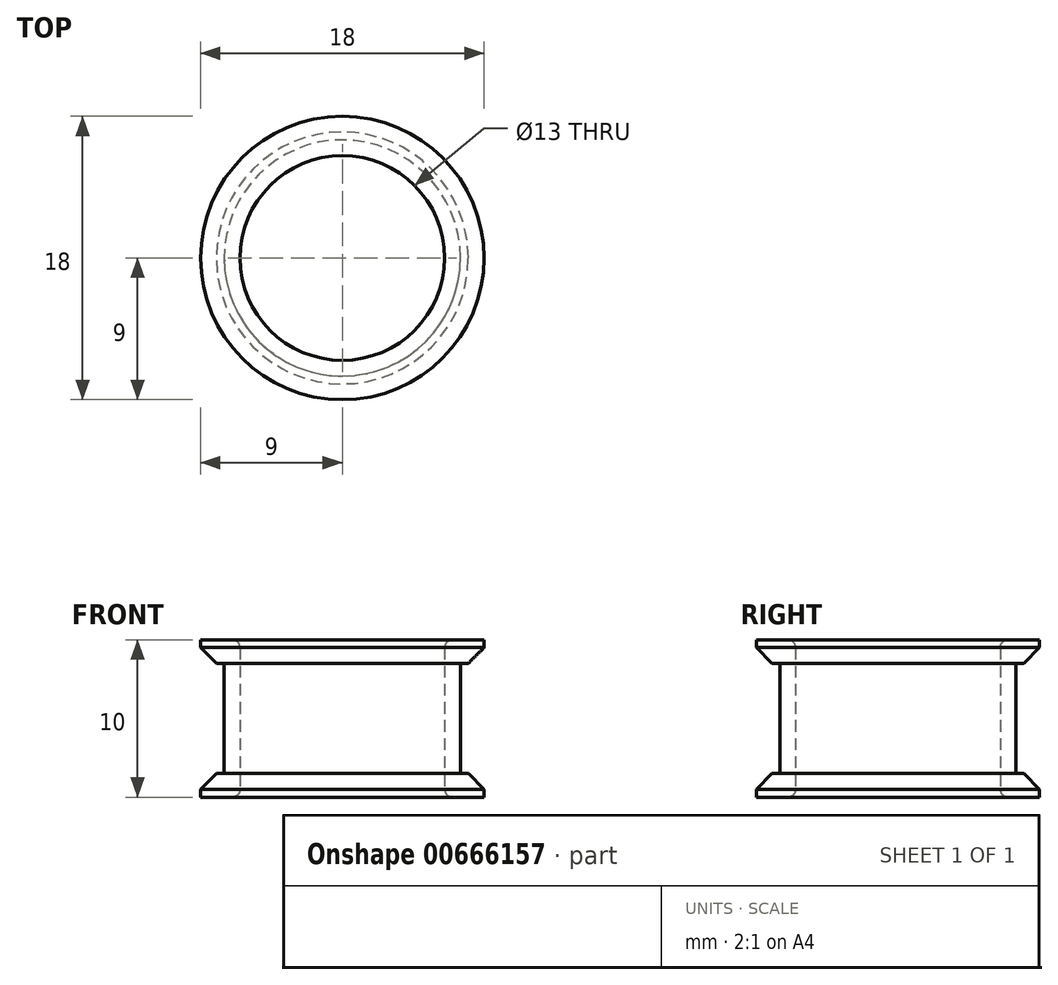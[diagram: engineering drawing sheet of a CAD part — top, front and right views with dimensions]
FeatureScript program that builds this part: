
annotation { "Feature Type Name" : "Feature", "Feature Type Description" : "" }
export const myFeature = defineFeature(function(context is Context, id is Id, definition is map)
    precondition{}
    {
        {
            var Q0;
            Q0=qCreatedBy(makeId("Top.planeOp"),FACE);
            var sketch = newSketch(context, id + "F0", { "sketchPlane" : qUnion([Q0])});
            skCircle(sketch, "E0", {"center": v(0, 0) * mm, "radius": 7.5 * mm});
            skCircle(sketch, "E1", {"center": v(0, 0) * mm, "radius": 6.5 * mm});
            skSolve(sketch);
        }
        {
            var Q0;
            Q0=makeQuery(id+"F0.imprint","IMPRINT",FACE,{"disambiguationData":[TD([[makeQuery(id+"F0.imprint","IMPRINT",EDGE,{"derivedFrom":sQuery(id+"F0.wireOp",EDGE,"E0")}),1.0]])]});
            extrude(context, id + "F1", {"entities" : qUnion([Q0]), "depth" : 10 * mm, "offsetDistance" : 25 * mm});
        }
        {
            var Q0;
            Q0=makeQuery(id+"F1.opExtrude","CAP_FACE",FACE,{"disambiguationData":[OSD([sQuery(id+"F0.wireOp",EDGE,"E0"),sQuery(id+"F0.wireOp",EDGE,"E1")])],"isStart":false});
            var sketch = newSketch(context, id + "F2", { "sketchPlane" : qUnion([Q0])});
            skCircle(sketch, "E2", {"center": v(0, 0) * mm, "radius": 9 * mm});
            skSolve(sketch);
        }
        {
            var Q0;
            Q0=makeQuery(id+"F2.imprint","IMPRINT",FACE,{"disambiguationData":[TD([[makeQuery(id+"F2.imprint","IMPRINT",EDGE,{"derivedFrom":sQuery(id+"F2.wireOp",EDGE,"E2")}),1.0]])]});
            extrude(context, id + "F3", {"entities" : qUnion([Q0]), "operationType" : NewBodyOperationType.ADD, "depth" : -1.5 * mm, "offsetDistance" : 25 * mm});
        }
        {
            var Q0;
            Q0=makeQuery(id+"F3.opExtrude","CAP_EDGE",EDGE,{"disambiguationData":[OSD([sQuery(id+"F2.wireOp",EDGE,"E2")])],"isStart":false});
            chamfer(context, id + "F4", {"entities" : qUnion([Q0]), "width" : 1 * mm, "tangentPropagation" : true});
        }
        {
            var Q0;
            Q0=makeQuery(id+"F1.opExtrude","CAP_FACE",FACE,{"disambiguationData":[OSD([sQuery(id+"F0.wireOp",EDGE,"E0"),sQuery(id+"F0.wireOp",EDGE,"E1")])],"isStart":true});
            var sketch = newSketch(context, id + "F5", { "sketchPlane" : qUnion([Q0])});
            skCircle(sketch, "E3", {"center": v(0, 0) * mm, "radius": 9 * mm});
            skSolve(sketch);
        }
        {
            var Q0;
            Q0 = qSketchRegion(id + "F5", true);
            var Q1;
            Q1=makeQuery(id+"F5.imprint","IMPRINT",FACE,{"disambiguationData":[TD([[makeQuery(id+"F5.imprint","IMPRINT",EDGE,{"derivedFrom":sQuery(id+"F5.wireOp",EDGE,"E3")}),1.0]])]});
            extrude(context, id + "F6", {"entities" : qUnion([Q0, Q1]), "operationType" : NewBodyOperationType.ADD, "depth" : -1.5 * mm, "offsetDistance" : 25 * mm});
        }
        {
            var Q0;
            Q0=makeQuery(id+"F6.opExtrude","CAP_EDGE",EDGE,{"disambiguationData":[OSD([sQuery(id+"F5.wireOp",EDGE,"E3")])],"isStart":false});
            chamfer(context, id + "F7", {"entities" : qUnion([Q0]), "width" : 1 * mm, "tangentPropagation" : true});
        }
        {
            var Q0;
            Q0=makeQuery(id+"F6.boolean.opBoolean","SPLIT",FACE,{"disambiguationData":[TD([makeQuery(id+"F1.opExtrude","SWEPT_FACE",FACE,{"disambiguationData":[OSD([sQuery(id+"F0.wireOp",EDGE,"E1")])]})])],"derivedFrom":makeQuery(id+"F6.opExtrude","CAP_FACE",FACE,{"disambiguationData":[OSD([sQuery(id+"F5.wireOp",EDGE,"E3")])],"isStart":false})});
            extrude(context, id + "F8", {"entities" : qUnion([Q0]), "operationType" : NewBodyOperationType.REMOVE, "oppositeDirection" : true, "depth" : 25 * mm, "offsetDistance" : 25 * mm});
        }
        {
            var Q0;
            {var subQ0=sQuery(id+"F5.wireOp",EDGE,"E3");var subQ1=sQuery(id+"F0.wireOp",EDGE,"E1");Q0=makeQuery(id+"F8.boolean.opBoolean","INTERSECT",EDGE,{"derivedFrom":[makeQuery(id+"F6.boolean.opBoolean","MERGE",FACE,{"derivedFrom":[makeQuery(id+"F1.opExtrude","CAP_FACE",FACE,{"disambiguationData":[OSD([sQuery(id+"F0.wireOp",EDGE,"E0"),subQ1])],"isStart":true}),makeQuery(id+"F6.opExtrude","CAP_FACE",FACE,{"disambiguationData":[OSD([subQ0])],"isStart":true})]}),makeQuery(id+"F8.opExtrude","SWEPT_FACE",FACE,{"disambiguationData":[OSD([subQ1,subQ0])]})]});}
            fillet(context, id + "F9", {"entities" : qUnion([Q0]), "radius" : 0.5 * mm, "tangentPropagation" : true, "allowEdgeOverflow" : false});
        }
        {
            var Q0;
            Q0=makeQuery(id+"F1.opExtrude","CAP_EDGE",EDGE,{"disambiguationData":[OSD([sQuery(id+"F0.wireOp",EDGE,"E1")])],"isStart":false});
            fillet(context, id + "F10", {"entities" : qUnion([Q0]), "radius" : 0.5 * mm, "tangentPropagation" : true, "allowEdgeOverflow" : false});
        }
    });
